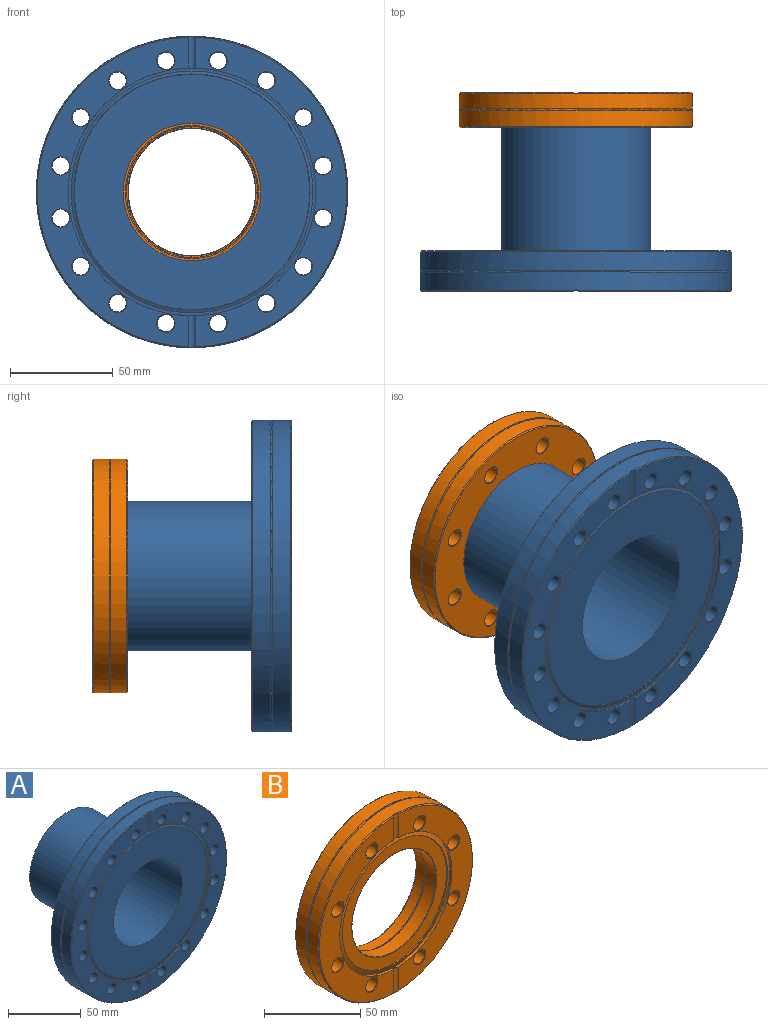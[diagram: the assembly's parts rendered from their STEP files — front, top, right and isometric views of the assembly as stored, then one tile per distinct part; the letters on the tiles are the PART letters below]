
ASSEMBLY  parts=2 mates=1
PART A: 67 faces, bbox 164.7x79.8x164.7 mm
  f0: plane 114.57x114.57mm, normal (0,-1,0), area 6782.8mm2, adj f1,f4
  f1: cone r=57.47mm half-angle=20deg, axis (0,-1,0), area 194.9mm2, adj f0,f2
  f2: cone r=60.32mm half-angle=70deg, axis (0,1,0), area 542.8mm2, adj f1,f3
  f3: plane 120.65x120.65mm, normal (0,-1,0), area 547.4mm2, adj f2,f5
  f4: cylinder r=33.5mm len=78.64mm, axis (0,1,0), area 16553.4mm2, adj f0,f66
  f5: cylinder r=60.32mm len=120.65mm, axis (0,1,0), area 439mm2, adj f3,f7,f9,f11,f14
  f6: cylinder r=75.82mm len=151.64mm, axis (0,-1,0), area 4267.5mm2, adj f7,f8,f10,f14,f64
  f7: cylinder r=2.38mm len=15.51mm, axis (0,0,1), area 61.4mm2, adj f5,f6,f8,f9,f10,f11
  f8: cone r=75.82mm half-angle=45deg, axis (0,1,0), area 168.5mm2, adj f6,f7,f9,f14
  f9: plane 150.58x73.54mm, normal (0,-1,0), area 2637.6mm2, adj f5,f7,f8,f14,f15,f18,f21,f24
  f10: cone r=75.82mm half-angle=45deg, axis (0,1,0), area 168.5mm2, adj f6,f7,f11,f14
  f11: plane 150.58x73.54mm, normal (0,-1,0), area 2637.6mm2, adj f5,f7,f10,f14,f39,f42,f45,f48
  f12: cylinder r=75.82mm len=151.64mm, axis (0,-1,0), area 4267.5mm2, adj f63,f64
  f13: plane 150.62x150.62mm, normal (0,1,0), area 12628.4mm2, adj f16,f19,f22,f25,f28,f31,f34,f37
  f14: cylinder r=2.38mm len=15.51mm, axis (0,0,-1), area 61.4mm2, adj f5,f6,f8,f9,f10,f11
  f15: cone r=4.47mm half-angle=45deg, axis (0,-1,0), area 9.8mm2, adj f9,f17
  f16: cone r=4.22mm half-angle=45deg, axis (0,1,0), area 9.8mm2, adj f13,f17
  f17: cylinder r=4.22mm len=19.3mm, axis (0,-1,0), area 511.4mm2, adj f15,f16
  f18: cone r=4.47mm half-angle=45deg, axis (0,-1,0), area 9.8mm2, adj f9,f20
  f19: cone r=4.22mm half-angle=45deg, axis (0,1,0), area 9.8mm2, adj f13,f20
  f20: cylinder r=4.22mm len=19.3mm, axis (0,-1,0), area 511.4mm2, adj f18,f19
  f21: cone r=4.47mm half-angle=45deg, axis (0,-1,0), area 9.8mm2, adj f9,f23
  f22: cone r=4.22mm half-angle=45deg, axis (0,1,0), area 9.8mm2, adj f13,f23
  f23: cylinder r=4.22mm len=19.3mm, axis (0,-1,0), area 511.4mm2, adj f21,f22
  f24: cone r=4.47mm half-angle=45deg, axis (0,-1,0), area 9.8mm2, adj f9,f26
  f25: cone r=4.22mm half-angle=45deg, axis (0,1,0), area 9.8mm2, adj f13,f26
  f26: cylinder r=4.22mm len=19.3mm, axis (0,-1,0), area 511.4mm2, adj f24,f25
  f27: cone r=4.47mm half-angle=45deg, axis (0,-1,0), area 9.8mm2, adj f9,f29
  f28: cone r=4.22mm half-angle=45deg, axis (0,1,0), area 9.8mm2, adj f13,f29
  f29: cylinder r=4.22mm len=19.3mm, axis (0,-1,0), area 511.4mm2, adj f27,f28
  f30: cone r=4.47mm half-angle=45deg, axis (0,-1,0), area 9.8mm2, adj f9,f32
  f31: cone r=4.22mm half-angle=45deg, axis (0,1,0), area 9.8mm2, adj f13,f32
  f32: cylinder r=4.22mm len=19.3mm, axis (0,-1,0), area 511.4mm2, adj f30,f31
  f33: cone r=4.47mm half-angle=45deg, axis (0,-1,0), area 9.8mm2, adj f9,f35
  f34: cone r=4.22mm half-angle=45deg, axis (0,1,0), area 9.8mm2, adj f13,f35
  f35: cylinder r=4.22mm len=19.3mm, axis (0,-1,0), area 511.4mm2, adj f33,f34
  f36: cone r=4.47mm half-angle=45deg, axis (0,-1,0), area 9.8mm2, adj f9,f38
  f37: cone r=4.22mm half-angle=45deg, axis (0,1,0), area 9.8mm2, adj f13,f38
  f38: cylinder r=4.22mm len=19.3mm, axis (0,-1,0), area 511.4mm2, adj f36,f37
  f39: cone r=4.47mm half-angle=45deg, axis (0,-1,0), area 9.8mm2, adj f11,f41
  f40: cone r=4.22mm half-angle=45deg, axis (0,1,0), area 9.8mm2, adj f13,f41
  f41: cylinder r=4.22mm len=19.3mm, axis (0,-1,0), area 511.4mm2, adj f39,f40
  f42: cone r=4.47mm half-angle=45deg, axis (0,-1,0), area 9.8mm2, adj f11,f44
  f43: cone r=4.22mm half-angle=45deg, axis (0,1,0), area 9.8mm2, adj f13,f44
  f44: cylinder r=4.22mm len=19.3mm, axis (0,-1,0), area 511.4mm2, adj f42,f43
  f45: cone r=4.47mm half-angle=45deg, axis (0,-1,0), area 9.8mm2, adj f11,f47
  f46: cone r=4.22mm half-angle=45deg, axis (0,1,0), area 9.8mm2, adj f13,f47
  f47: cylinder r=4.22mm len=19.3mm, axis (0,-1,0), area 511.4mm2, adj f45,f46
  f48: cone r=4.47mm half-angle=45deg, axis (0,-1,0), area 9.8mm2, adj f11,f50
  f49: cone r=4.22mm half-angle=45deg, axis (0,1,0), area 9.8mm2, adj f13,f50
  f50: cylinder r=4.22mm len=19.3mm, axis (0,-1,0), area 511.4mm2, adj f48,f49
  f51: cone r=4.47mm half-angle=45deg, axis (0,-1,0), area 9.8mm2, adj f11,f53
  f52: cone r=4.22mm half-angle=45deg, axis (0,1,0), area 9.8mm2, adj f13,f53
  f53: cylinder r=4.22mm len=19.3mm, axis (0,-1,0), area 511.4mm2, adj f51,f52
  f54: cone r=4.47mm half-angle=45deg, axis (0,-1,0), area 9.8mm2, adj f11,f56
  f55: cone r=4.22mm half-angle=45deg, axis (0,1,0), area 9.8mm2, adj f13,f56
  f56: cylinder r=4.22mm len=19.3mm, axis (0,-1,0), area 511.4mm2, adj f54,f55
  f57: cone r=4.47mm half-angle=45deg, axis (0,-1,0), area 9.8mm2, adj f11,f59
  f58: cone r=4.22mm half-angle=45deg, axis (0,1,0), area 9.8mm2, adj f13,f59
  f59: cylinder r=4.22mm len=19.3mm, axis (0,-1,0), area 511.4mm2, adj f57,f58
  f60: cone r=4.47mm half-angle=45deg, axis (0,-1,0), area 9.8mm2, adj f11,f62
  f61: cone r=4.22mm half-angle=45deg, axis (0,1,0), area 9.8mm2, adj f13,f62
  f62: cylinder r=4.22mm len=19.3mm, axis (0,-1,0), area 511.4mm2, adj f60,f61
  f63: cone r=75.31mm half-angle=45deg, axis (0,-1,0), area 341.1mm2, adj f12,f13
  f64: torus R=76.07mm, axis (0,-1,0), area 505.7mm2, adj f6,f12
  f65: cylinder r=36.5mm len=73mm, axis (0,-1,0), area 13760.2mm2, adj f13,f66
  f66: plane 73x73mm, normal (0,1,0), area 659.7mm2, adj f4,f65
PART B: 47 faces, bbox 123.4x17.3x123.4 mm
  f0: cylinder r=56.77mm len=113.54mm, axis (0,-1,0), area 2742.3mm2, adj f1,f2,f5,f11,f42
  f1: cylinder r=2.38mm len=15.52mm, axis (0,0,1), area 61.5mm2, adj f0,f2,f3,f4,f5,f6
  f2: cone r=56.77mm half-angle=45deg, axis (0,1,0), area 125.5mm2, adj f0,f1,f3,f11
  f3: plane 112.47x54.49mm, normal (0,-1,0), area 1991.8mm2, adj f1,f2,f4,f11,f12,f15,f18,f21
  f4: cylinder r=41.27mm len=82.55mm, axis (0,1,0), area 423mm2, adj f1,f3,f6,f11,f44
  f5: cone r=56.77mm half-angle=45deg, axis (0,1,0), area 125.5mm2, adj f0,f1,f6,f11
  f6: plane 112.47x54.49mm, normal (0,-1,0), area 1991.8mm2, adj f1,f4,f5,f11,f24,f27,f30,f33
  f7: cylinder r=56.77mm len=113.54mm, axis (0,-1,0), area 2742.3mm2, adj f39,f42
  f8: plane 112.52x112.52mm, normal (0,1,0), area 6147mm2, adj f13,f16,f19,f22,f25,f28,f31,f34
  f9: cylinder r=31.88mm len=63.75mm, axis (0,1,0), area 1229.6mm2, adj f36,f41
  f10: cylinder r=30.99mm len=61.98mm, axis (0,-1,0), area 1538mm2, adj f37,f38
  f11: cylinder r=2.38mm len=15.52mm, axis (0,0,-1), area 61.5mm2, adj f0,f2,f3,f4,f5,f6
  f12: cone r=4.47mm half-angle=45deg, axis (0,-1,0), area 9.8mm2, adj f3,f14
  f13: cone r=4.22mm half-angle=45deg, axis (0,1,0), area 9.8mm2, adj f8,f14
  f14: cylinder r=4.22mm len=16.76mm, axis (0,-1,0), area 444.1mm2, adj f12,f13
  f15: cone r=4.47mm half-angle=45deg, axis (0,-1,0), area 9.8mm2, adj f3,f17
  f16: cone r=4.22mm half-angle=45deg, axis (0,1,0), area 9.8mm2, adj f8,f17
  f17: cylinder r=4.22mm len=16.76mm, axis (0,-1,0), area 444.1mm2, adj f15,f16
  f18: cone r=4.47mm half-angle=45deg, axis (0,-1,0), area 9.8mm2, adj f3,f20
  f19: cone r=4.22mm half-angle=45deg, axis (0,1,0), area 9.8mm2, adj f8,f20
  f20: cylinder r=4.22mm len=16.76mm, axis (0,-1,0), area 444.1mm2, adj f18,f19
  f21: cone r=4.47mm half-angle=45deg, axis (0,-1,0), area 9.8mm2, adj f3,f23
  f22: cone r=4.22mm half-angle=45deg, axis (0,1,0), area 9.8mm2, adj f8,f23
  f23: cylinder r=4.22mm len=16.76mm, axis (0,-1,0), area 444.1mm2, adj f21,f22
  f24: cone r=4.47mm half-angle=45deg, axis (0,-1,0), area 9.8mm2, adj f6,f26
  f25: cone r=4.22mm half-angle=45deg, axis (0,1,0), area 9.8mm2, adj f8,f26
  f26: cylinder r=4.22mm len=16.76mm, axis (0,-1,0), area 444.1mm2, adj f24,f25
  f27: cone r=4.47mm half-angle=45deg, axis (0,-1,0), area 9.8mm2, adj f6,f29
  f28: cone r=4.22mm half-angle=45deg, axis (0,1,0), area 9.8mm2, adj f8,f29
  f29: cylinder r=4.22mm len=16.76mm, axis (0,-1,0), area 444.1mm2, adj f27,f28
  f30: cone r=4.47mm half-angle=45deg, axis (0,-1,0), area 9.8mm2, adj f6,f32
  f31: cone r=4.22mm half-angle=45deg, axis (0,1,0), area 9.8mm2, adj f8,f32
  f32: cylinder r=4.22mm len=16.76mm, axis (0,-1,0), area 444.1mm2, adj f30,f31
  f33: cone r=4.47mm half-angle=45deg, axis (0,-1,0), area 9.8mm2, adj f6,f35
  f34: cone r=4.22mm half-angle=45deg, axis (0,1,0), area 9.8mm2, adj f8,f35
  f35: cylinder r=4.22mm len=16.76mm, axis (0,-1,0), area 444.1mm2, adj f33,f34
  f36: torus R=32.38mm, axis (0,1,0), area 160.7mm2, adj f8,f9
  f37: torus R=31.19mm, axis (0,-1,0), area 62.3mm2, adj f10,f46
  f38: torus R=31.24mm, axis (0,1,0), area 77.9mm2, adj f10,f45
  f39: cone r=56.26mm half-angle=45deg, axis (0,-1,0), area 255.1mm2, adj f7,f8
  f40: torus R=31.88mm, axis (0,-1,0), area 163.9mm2, adj f41,f46
  f41: cone r=31.88mm half-angle=32deg, axis (0,-1,0), area 122.7mm2, adj f9,f40
  f42: torus R=57.02mm, axis (0,-1,0), area 378.4mm2, adj f0,f7
  f43: cone r=38.61mm half-angle=20deg, axis (0,-1,0), area 130.8mm2, adj f44,f45
  f44: cone r=41.27mm half-angle=70deg, axis (0,1,0), area 712.3mm2, adj f4,f43
  f45: plane 76.85x76.85mm, normal (0,-1,0), area 1571.7mm2, adj f38,f43
  f46: plane 63.75x63.75mm, normal (0,1,0), area 135.9mm2, adj f37,f40
PLACE A at identity
PLACE B rot(axis=(1,0,0),180deg) t=(0,78.54,0)mm
MATE fastened B.f9 <-> A.f6  axis (0,-1,0) through (0,69.91,0)mm
